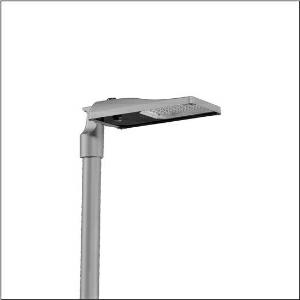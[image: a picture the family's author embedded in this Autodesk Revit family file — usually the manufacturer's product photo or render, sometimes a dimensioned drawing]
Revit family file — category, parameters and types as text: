
# Revit family: streetlight_sl_31_mini___st1_0a_5xh6d3at08ga_a0b3
name_source: partatom
category: Lighting Fixtures
units: mm (PartAtom-declared; Revit-internal decimal feet)

## family parameters
Cut with Voids When Loaded = No
Host = Face
Light Source = No
Part Type = Normal
Room Calculation Point = No
Round Connector Dimension = Use Diameter
Shared = No

## types (1)
- --- (1 x LED, 5880 lm, 39.3 W, 3000K)
    Apparent Load = 39 VA
    CIE Flux Codes = 37 72 97 100 100
    Color Rendering = 70
    Color Temperature = 3000K
    Default Elevation = 1800 mm
    Description = Streetlight SL 31 mini D4i mast luminaire for post-top, side-entry; light control with lens of PMMA; light distribution: ST1.0a, direct asymmetric distribution, for standard-compliant lighting for roads and squares; LED: luminous flux: 5.880lm, light colour: 730, colour temperature: 3000K; luminous efficacy: 149,6lm/W; control: pre-setting: logarithmic dimming characteristic, flexible luminous flux parameterisation, time-dependent luminous flux control, constant luminous flux control, power reduction, intelligent temperature release in ECG and LED module, overheat protection; luminaire housing, of diecast aluminium, SITECO metallic grey (DB 702S), corrosivity category C5 high according to DIN EN ISO 12944; cover of toughened safety glass, transparent, opened without tools; mast flange of diecast aluminium, SITECO metallic grey (DB 702S), spigot size: 76/60mm, mast flange included unmounted; cable length: 6,5m, connection cable pre-assembled; mains connection: 220..240V, AC, 50/60Hz; power consumption (at start of service life): 39,3W / (at end of service life): 40,7W / (with reduced operation 50%): 18,1W; protection rating (complete): IP66; insulation class (complete): insulation class II (safety insulation); impact resistance: IK09; certification: CE, ENEC, ENEC+, VDE, UKCA, ZD4i; permissible operating ambient temperature for outdoor applications: -40..+50°C; packaging unit: 1 piece

Light Distribution: ST1.0a
    Height = 76 mm
    Lamp = 1 x LED
    Lamp Light Flux = 5880 lm
    Lamp Power = 39.3 W
    Lamp count = 1
    Length = 547 mm
    Luminous efficacy = 150 lm/W
    Manufacturer = Siteco
    ModVariant = No
    Model = 5XH6D3AT08GA
    Number of Poles = 1
    OnlyDefault = Yes
    Power Factor = 1
    Product Name = Streetlight SL 31 mini | ST1.0a
    Product group = mast luminaire | pylon top
    ProductGroupID = 6100
    Protection Class = Protection class II
    Protection Degree = IP 66
    RLX_Detail_Level = 1
    RLX_Emergency_Light_Flux = 0 lm
    RLX_Emergency_Type = 0
    RLX_Emergency_Type_DB = No
    RlxData = <blob elided: 39773 chars, md5=874dcf15>
    Socket = socket
    Standby Power = 0 W
    System Light Flux = 5880 lm
    System Power = 39 W
    Type Comments = factory setting: luminous flux: 100 % | dim-lin: 254 | 798 mA
    Type Image = l_1300332.jpg
    URL = http://relux.com
    VarID = @adj_060585
    Voltage = 0 V
    Weight = 0.00 kg
    Width = 265 mm

## geometry (parser evidence)
native form markers: Blend x4, Sweep x10
no freeform markers — native parametric forms only
